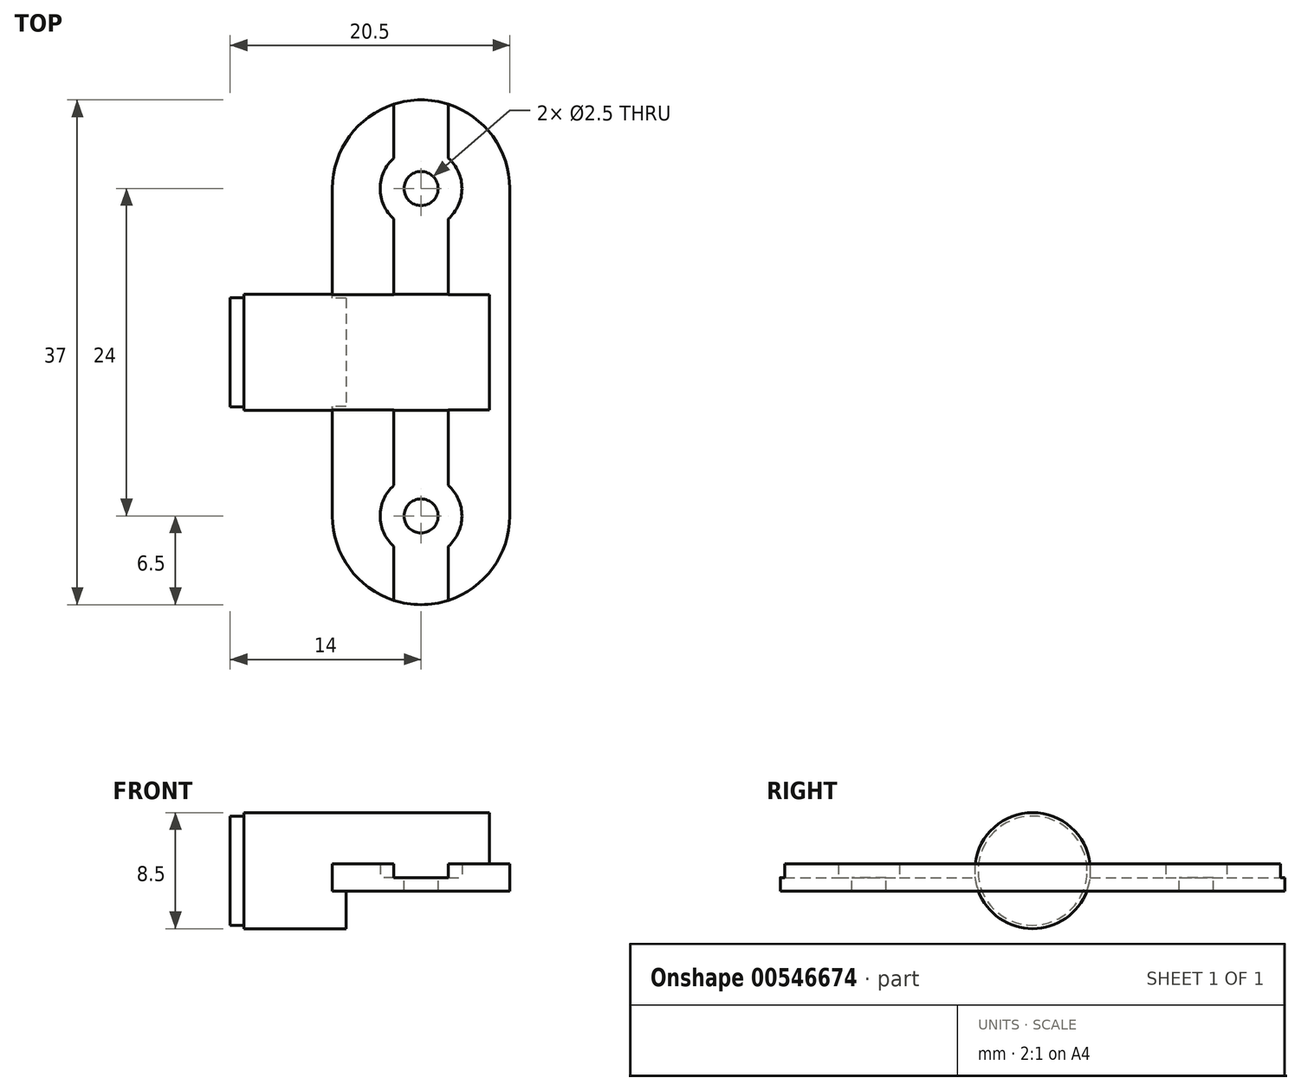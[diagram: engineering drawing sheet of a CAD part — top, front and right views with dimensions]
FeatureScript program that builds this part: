
annotation { "Feature Type Name" : "Feature", "Feature Type Description" : "" }
export const myFeature = defineFeature(function(context is Context, id is Id, definition is map)
    precondition{}
    {
        {
            var Q0;
            Q0=qCreatedBy(makeId("Top.planeOp"),FACE);
            var sketch = newSketch(context, id + "F0", { "sketchPlane" : qUnion([Q0])});
            skLineSegment(sketch, "E0.bottom", {"start": v(0, 18.5) * mm, "end": v(0, 18.5) * mm});
            skLineSegment(sketch, "E0.top", {"start": v(0, -18.5) * mm, "end": v(0, -18.5) * mm});
            skLineSegment(sketch, "E0.left", {"start": v(-6.5, 12) * mm, "end": v(-6.5, -12) * mm});
            skLineSegment(sketch, "E0.right", {"start": v(6.5, 12) * mm, "end": v(6.5, -12) * mm});
            skPoint(sketch, "E1.visualSharp", {"position": v(-6.5, 18.5) * mm});
            skArc(sketch, "E1.filletArc", {"start": v(0, 18.5) * mm, "mid": v(-4.6, 16.6) * mm, "end": v(-6.5, 12) * mm});
            skPoint(sketch, "E2.visualSharp", {"position": v(6.5, 18.5) * mm});
            skArc(sketch, "E2.filletArc", {"start": v(6.5, 12) * mm, "mid": v(4.6, 16.6) * mm, "end": v(0, 18.5) * mm});
            skPoint(sketch, "E3.visualSharp", {"position": v(6.5, -18.5) * mm});
            skArc(sketch, "E3.filletArc", {"start": v(0, -18.5) * mm, "mid": v(4.6, -16.6) * mm, "end": v(6.5, -12) * mm});
            skPoint(sketch, "E4.visualSharp", {"position": v(-6.5, -18.5) * mm});
            skArc(sketch, "E4.filletArc", {"start": v(-6.5, -12) * mm, "mid": v(-4.6, -16.6) * mm, "end": v(0, -18.5) * mm});
            skSolve(sketch);
        }
        {
            var Q0;
            Q0=qSketchRegion(id+"F0",true);
            extrude(context, id + "F1", {"entities" : qUnion([Q0]), "depth" : 2 * mm});
        }
        {
            var Q0;
            Q0=makeQuery(id+"F1.opExtrude","CAP_FACE",FACE,{"disambiguationData":[OSD([sQuery(id+"F0.wireOp",EDGE,"E0.left"),sQuery(id+"F0.wireOp",EDGE,"E0.right"),sQuery(id+"F0.wireOp",EDGE,"E1.filletArc"),sQuery(id+"F0.wireOp",EDGE,"E2.filletArc"),sQuery(id+"F0.wireOp",EDGE,"E3.filletArc"),sQuery(id+"F0.wireOp",EDGE,"E4.filletArc")])],"isStart":false});
            var sketch = newSketch(context, id + "F2", { "sketchPlane" : qUnion([Q0])});
            skLineSegment(sketch, "E5", {"start": v(2, -20.14) * mm, "end": v(2, 20.65) * mm});
            skLineSegment(sketch, "E6.MirrorCS", {"start": v(-2, -20.14) * mm, "end": v(-2, 20.65) * mm});
            skLineSegment(sketch, "E7", {"start": v(2, -20.14) * mm, "end": v(-2, -20.14) * mm});
            skLineSegment(sketch, "E8", {"start": v(2, 20.65) * mm, "end": v(-2, 20.65) * mm});
            skSolve(sketch);
        }
        {
            var Q0;
            Q0=qSketchRegion(id+"F2",true);
            extrude(context, id + "F3", {"entities" : qUnion([Q0]), "operationType" : NewBodyOperationType.REMOVE, "oppositeDirection" : true, "depth" : 1 * mm});
        }
        {
            var Q0;
            Q0=qCreatedBy(makeId("Right.planeOp"),FACE);
            cPlane(context, id + "F4", {"entities" : qUnion([Q0]), "cplaneType" : CPlaneType.OFFSET, "offset" : 14 * mm, "oppositeDirection" : true, "width" : 150 * mm, "height" : 150 * mm});
        }
        {
            var Q0;
            Q0=qCreatedBy(id+"F4.planeOp",FACE);
            var sketch = newSketch(context, id + "F5", { "sketchPlane" : qUnion([Q0])});
            skCircle(sketch, "E9", {"center": v(0, 1.5) * mm, "radius": 4.25 * mm});
            skSolve(sketch);
        }
        {
            var Q0;
            Q0=qSketchRegion(id+"F5",true);
            extrude(context, id + "F6", {"entities" : qUnion([Q0]), "operationType" : NewBodyOperationType.ADD, "depth" : 19 * mm});
        }
        {
            var Q0;
            Q0=makeQuery(id+"F6.opExtrude","CAP_FACE",FACE,{"disambiguationData":[OSD([sQuery(id+"F5.wireOp",EDGE,"E9")])],"isStart":true});
            var sketch = newSketch(context, id + "F7", { "sketchPlane" : qUnion([Q0])});
            skLineSegment(sketch, "E10", {"start": v(-2.53, 1.5) * mm, "end": v(2.09, 1.5) * mm});
            skCircle(sketch, "E11", {"center": v(0, 1.5) * mm, "radius": 4 * mm});
            skCircle(sketch, "E12", {"center": v(0, 1.5) * mm, "radius": 4.4 * mm});
            skSolve(sketch);
        }
        {
            var Q0;
            Q0=makeQuery(id+"F7.imprint","IMPRINT",FACE,{"disambiguationData":[TD([[makeQuery(id+"F7.imprint","IMPRINT",EDGE,{"derivedFrom":sQuery(id+"F7.wireOp",EDGE,"E12")}),1.0]])]});
            var Q1;
            Q1=makeQuery(id+"F7.imprint","IMPRINT",FACE,{"disambiguationData":[TD([[makeQuery(id+"F7.imprint","IMPRINT",EDGE,{"derivedFrom":sQuery(id+"F7.wireOp",EDGE,"E11")}),-1.0]])]});
            extrude(context, id + "F8", {"entities" : qUnion([Q0, Q1]), "operationType" : NewBodyOperationType.REMOVE, "oppositeDirection" : true, "depth" : 1 * mm});
        }
        {
            var Q0;
            Q0=makeQuery(id+"F1.opExtrude","CAP_FACE",FACE,{"disambiguationData":[OSD([sQuery(id+"F0.wireOp",EDGE,"E0.left"),sQuery(id+"F0.wireOp",EDGE,"E0.right"),sQuery(id+"F0.wireOp",EDGE,"E1.filletArc"),sQuery(id+"F0.wireOp",EDGE,"E2.filletArc"),sQuery(id+"F0.wireOp",EDGE,"E3.filletArc"),sQuery(id+"F0.wireOp",EDGE,"E4.filletArc")])],"isStart":true});
            var sketch = newSketch(context, id + "F9", { "sketchPlane" : qUnion([Q0])});
            skLineSegment(sketch, "E13", {"start": v(-5.5, 5.94) * mm, "end": v(6.5, 5.94) * mm});
            skLineSegment(sketch, "E14", {"start": v(6.5, 5.94) * mm, "end": v(6.5, -7.05) * mm});
            skLineSegment(sketch, "E15", {"start": v(6.5, -7.05) * mm, "end": v(-5.5, -7.05) * mm});
            skLineSegment(sketch, "E16.0", {"start": v(-5.5, -7.05) * mm, "end": v(-5.5, 5.94) * mm});
            skSolve(sketch);
        }
        {
            var Q0;
            Q0=qSketchRegion(id+"F9",true);
            extrude(context, id + "F10", {"entities" : qUnion([Q0]), "operationType" : NewBodyOperationType.REMOVE, "depth" : 25 * mm});
        }
        {
            var Q0;
            {var subQ0=sQuery(id+"F2.wireOp",EDGE,"E5");var subQ1=sQuery(id+"F2.wireOp",EDGE,"E6.MirrorCS");Q0=makeQuery(id+"F6.boolean.opBoolean","SPLIT",FACE,{"disambiguationData":[TD([makeQuery(id+"F1.opExtrude","SWEPT_FACE",FACE,{"disambiguationData":[OSD([sQuery(id+"F0.wireOp",EDGE,"E3.filletArc"),sQuery(id+"F0.wireOp",EDGE,"E4.filletArc")])]})])],"derivedFrom":makeQuery(id+"F3.boolean.opBoolean","COPY",FACE,{"derivedFrom":makeQuery(id+"F3.opExtrude","CAP_FACE",FACE,{"disambiguationData":[OSD([subQ0,subQ1,sQuery(id+"F2.wireOp",EDGE,"E7"),sQuery(id+"F2.wireOp",EDGE,"E8")])],"isStart":false})})});}
            var sketch = newSketch(context, id + "F11", { "sketchPlane" : qUnion([Q0])});
            skCircle(sketch, "E17", {"center": v(0, -12) * mm, "radius": 3 * mm});
            skCircle(sketch, "E18.MirrorC", {"center": v(0, 12) * mm, "radius": 3 * mm});
            skSolve(sketch);
        }
        {
            var Q0;
            Q0=qSketchRegion(id+"F11",true);
            var Q1;
            {var subQ0=sQuery(id+"F0.wireOp",EDGE,"E0.left");var subQ1=makeQuery(id+"F1.opExtrude","SWEPT_FACE",FACE,{"disambiguationData":[OSD([subQ0])]});var subQ2=sQuery(id+"F0.wireOp",EDGE,"E2.filletArc");var subQ3=sQuery(id+"F0.wireOp",EDGE,"E1.filletArc");var subQ4=makeQuery(id+"F1.opExtrude","SWEPT_FACE",FACE,{"disambiguationData":[OSD([subQ3,subQ2])]});var subQ6=sQuery(id+"F0.wireOp",EDGE,"E4.filletArc");var subQ7=sQuery(id+"F0.wireOp",EDGE,"E3.filletArc");Q1=makeQuery(id+"F6.boolean.opBoolean","SPLIT",FACE,{"disambiguationData":[TD([subQ4])],"derivedFrom":makeQuery(id+"F3.boolean.opBoolean","SPLIT",FACE,{"disambiguationData":[TD([subQ1])],"derivedFrom":makeQuery(id+"F1.opExtrude","CAP_FACE",FACE,{"disambiguationData":[OSD([subQ0,sQuery(id+"F0.wireOp",EDGE,"E0.right"),subQ3,subQ2,subQ7,subQ6])],"isStart":false})})});}
            extrude(context, id + "F12", {"entities" : qUnion([Q0]), "operationType" : NewBodyOperationType.REMOVE, "endBound" : BoundingType.UP_TO_SURFACE, "endBoundEntityFace" : qUnion([Q1]), "depth" : 25 * mm});
        }
        {
            var Q0;
            {var subQ0=sQuery(id+"F2.wireOp",EDGE,"E5");var subQ1=sQuery(id+"F2.wireOp",EDGE,"E6.MirrorCS");Q0=makeQuery(id+"F12.boolean.opBoolean","MERGE",FACE,{"derivedFrom":[makeQuery(id+"F6.boolean.opBoolean","SPLIT",FACE,{"disambiguationData":[TD([makeQuery(id+"F1.opExtrude","SWEPT_FACE",FACE,{"disambiguationData":[OSD([sQuery(id+"F0.wireOp",EDGE,"E3.filletArc"),sQuery(id+"F0.wireOp",EDGE,"E4.filletArc")])]})])],"derivedFrom":makeQuery(id+"F3.boolean.opBoolean","COPY",FACE,{"derivedFrom":makeQuery(id+"F3.opExtrude","CAP_FACE",FACE,{"disambiguationData":[OSD([subQ0,subQ1,sQuery(id+"F2.wireOp",EDGE,"E7"),sQuery(id+"F2.wireOp",EDGE,"E8")])],"isStart":false})})}),makeQuery(id+"F12.opExtrude","CAP_FACE",FACE,{"disambiguationData":[OSD([sQuery(id+"F11.wireOp",EDGE,"E17")])],"isStart":true})]});}
            var sketch = newSketch(context, id + "F13", { "sketchPlane" : qUnion([Q0])});
            skCircle(sketch, "E19", {"center": v(0, -12) * mm, "radius": 1.25 * mm});
            skSolve(sketch);
        }
        {
            var Q0;
            Q0=qSketchRegion(id+"F13",true);
            extrude(context, id + "F14", {"entities" : qUnion([Q0]), "operationType" : NewBodyOperationType.REMOVE, "endBound" : BoundingType.THROUGH_ALL, "oppositeDirection" : true, "depth" : 25 * mm});
        }
        {
            var Q0;
            {var subQ0=sQuery(id+"F2.wireOp",EDGE,"E5");var subQ1=sQuery(id+"F2.wireOp",EDGE,"E6.MirrorCS");Q0=makeQuery(id+"F12.boolean.opBoolean","MERGE",FACE,{"derivedFrom":[makeQuery(id+"F6.boolean.opBoolean","SPLIT",FACE,{"disambiguationData":[TD([makeQuery(id+"F1.opExtrude","SWEPT_FACE",FACE,{"disambiguationData":[OSD([sQuery(id+"F0.wireOp",EDGE,"E1.filletArc"),sQuery(id+"F0.wireOp",EDGE,"E2.filletArc")])]})])],"derivedFrom":makeQuery(id+"F3.boolean.opBoolean","COPY",FACE,{"derivedFrom":makeQuery(id+"F3.opExtrude","CAP_FACE",FACE,{"disambiguationData":[OSD([subQ0,subQ1,sQuery(id+"F2.wireOp",EDGE,"E7"),sQuery(id+"F2.wireOp",EDGE,"E8")])],"isStart":false})})}),makeQuery(id+"F12.opExtrude","CAP_FACE",FACE,{"disambiguationData":[OSD([sQuery(id+"F11.wireOp",EDGE,"E18.MirrorC")])],"isStart":true})]});}
            var sketch = newSketch(context, id + "F15", { "sketchPlane" : qUnion([Q0])});
            skCircle(sketch, "E20", {"center": v(0, 12) * mm, "radius": 1.25 * mm});
            skSolve(sketch);
        }
        {
            var Q0;
            Q0=qSketchRegion(id+"F15",true);
            extrude(context, id + "F16", {"entities" : qUnion([Q0]), "operationType" : NewBodyOperationType.REMOVE, "endBound" : BoundingType.THROUGH_ALL, "oppositeDirection" : true, "depth" : 25 * mm});
        }
    });
